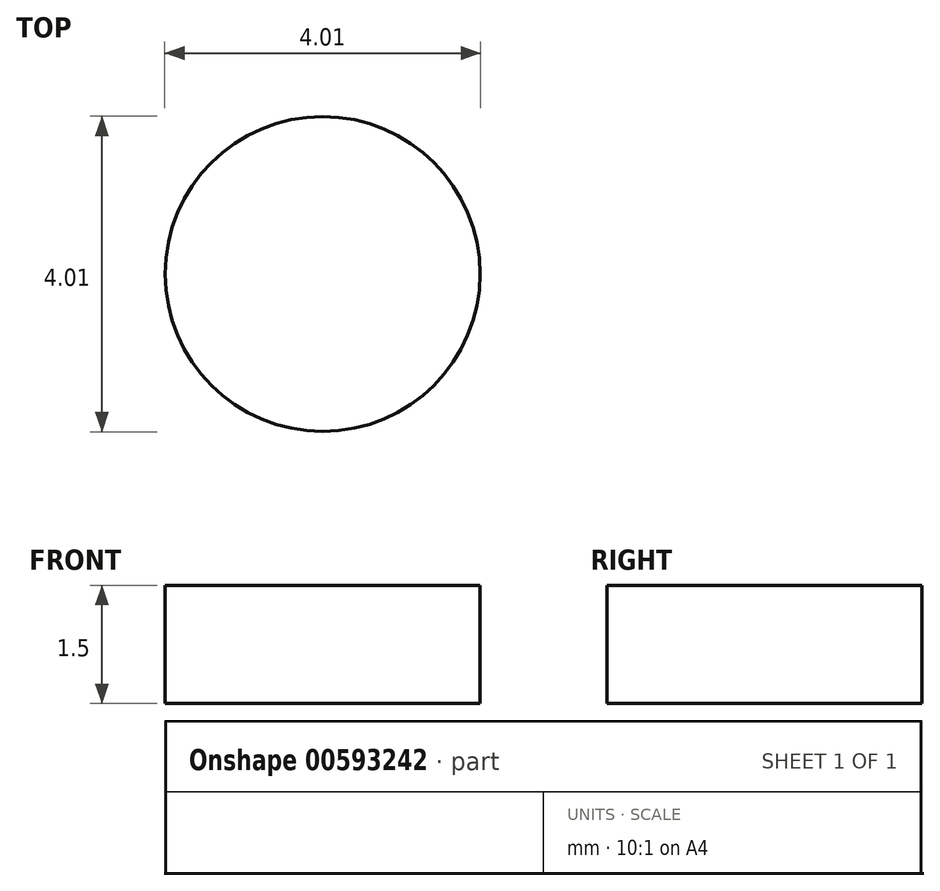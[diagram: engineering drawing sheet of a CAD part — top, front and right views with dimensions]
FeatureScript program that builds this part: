
annotation { "Feature Type Name" : "Feature", "Feature Type Description" : "" }
export const myFeature = defineFeature(function(context is Context, id is Id, definition is map)
    precondition{}
    {
        {
            var Q0;
            Q0=qCreatedBy(makeId("Front.planeOp"),FACE);
            var sketch = newSketch(context, id + "F0", { "sketchPlane" : qUnion([Q0])});
            skLineSegment(sketch, "E0", {"start": v(0, 20) * mm, "end": v(0, 0) * mm});
            skLineSegment(sketch, "E1", {"start": v(0, 0) * mm, "end": v(20, 0) * mm});
            skLineSegment(sketch, "E2", {"start": v(20, 0) * mm, "end": v(20, 1.5) * mm});
            skLineSegment(sketch, "E3", {"start": v(20, 1.5) * mm, "end": v(1.75, 1.5) * mm});
            skLineSegment(sketch, "E4", {"start": v(1.5, 1.75) * mm, "end": v(1.5, 20) * mm});
            skLineSegment(sketch, "E5", {"start": v(1.5, 20) * mm, "end": v(0, 20) * mm});
            skPoint(sketch, "E6.visualSharp", {"position": v(1.5, 1.5) * mm});
            skArc(sketch, "E6.filletArc", {"start": v(1.5, 1.75) * mm, "mid": v(1.57, 1.57) * mm, "end": v(1.75, 1.5) * mm});
            skSolve(sketch);
        }
        {
            var Q0;
            Q0=qSketchRegion(id+"F0",true);
            extrude(context, id + "F1", {"entities" : qUnion([Q0]), "endBound" : BoundingType.SYMMETRIC, "depth" : 38.1 * mm});
        }
        {
            var Q0;
            Q0=makeQuery(id+"F1.opExtrude","SWEPT_FACE",FACE,{"disambiguationData":[OSD([sQuery(id+"F0.wireOp",EDGE,"E0")])]});
            var sketch = newSketch(context, id + "F2", { "sketchPlane" : qUnion([Q0])});
            skCircle(sketch, "E7", {"center": v(9.53, 8.57) * mm, "radius": 3.18 * mm});
            skCircle(sketch, "E8", {"center": v(-9.53, 5.72) * mm, "radius": 2 * mm});
            skSolve(sketch);
        }
        {
            var Q0;
            Q0=qSketchRegion(id+"F2",true);
            extrude(context, id + "F3", {"entities" : qUnion([Q0]), "operationType" : NewBodyOperationType.REMOVE, "endBound" : BoundingType.UP_TO_NEXT, "oppositeDirection" : true, "depth" : 25.4 * mm});
        }
        {
            var Q0;
            Q0=makeQuery(id+"F1.opExtrude","SWEPT_FACE",FACE,{"disambiguationData":[OSD([sQuery(id+"F0.wireOp",EDGE,"E1")])]});
            var sketch = newSketch(context, id + "F4", { "sketchPlane" : qUnion([Q0])});
            skCircle(sketch, "E9", {"center": v(8.57, 9.53) * mm, "radius": 3.18 * mm});
            skCircle(sketch, "E10.MirrorC", {"center": v(5.72, -9.53) * mm, "radius": 2 * mm});
            skSolve(sketch);
        }
        {
            var Q0;
            Q0=makeQuery(id+"F4.imprint","IMPRINT",FACE,{"disambiguationData":[TD([[makeQuery(id+"F4.imprint","IMPRINT",EDGE,{"derivedFrom":sQuery(id+"F4.wireOp",EDGE,"E9")}),1.0]])]});
            var Q1;
            Q1=makeQuery(id+"F4.imprint","IMPRINT",FACE,{"disambiguationData":[TD([[makeQuery(id+"F4.imprint","IMPRINT",EDGE,{"derivedFrom":sQuery(id+"F4.wireOp",EDGE,"E10.MirrorC")}),-1.0]])]});
            extrude(context, id + "F5", {"entities" : qUnion([Q0, Q1]), "operationType" : NewBodyOperationType.REMOVE, "endBound" : BoundingType.UP_TO_NEXT, "oppositeDirection" : true, "depth" : 25.4 * mm});
        }
    });
